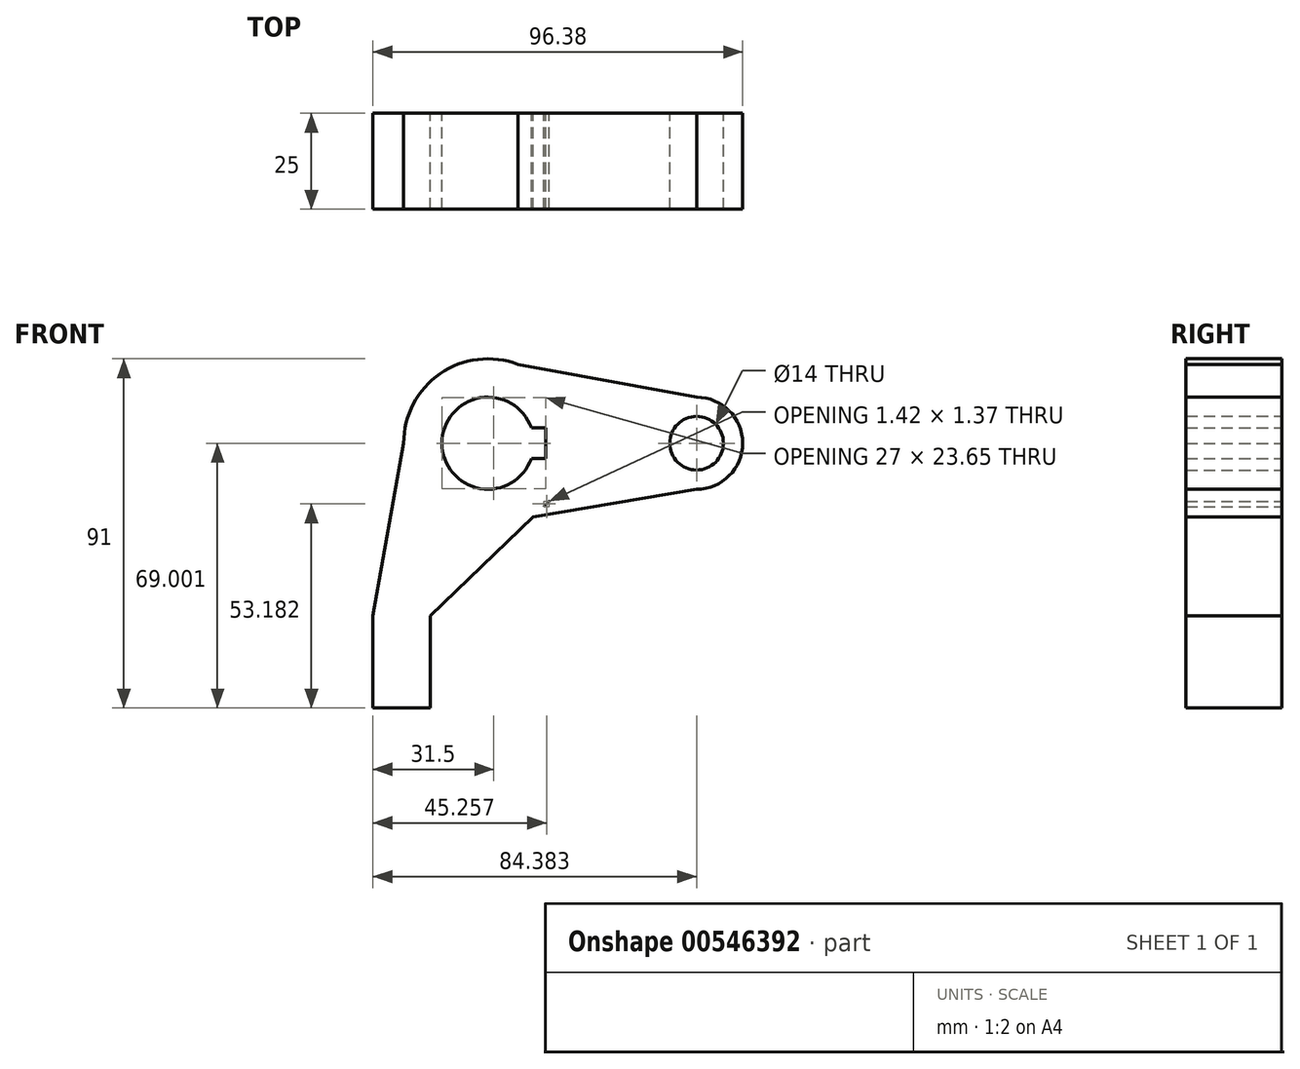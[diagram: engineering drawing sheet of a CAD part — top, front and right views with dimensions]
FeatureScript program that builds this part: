
annotation { "Feature Type Name" : "Feature", "Feature Type Description" : "" }
export const myFeature = defineFeature(function(context is Context, id is Id, definition is map)
    precondition{}
    {
        {
            var Q0;
            Q0=qCreatedBy(makeId("Front.planeOp"),FACE);
            var sketch = newSketch(context, id + "F0", { "sketchPlane" : qUnion([Q0])});
            skCircle(sketch, "E0", {"center": v(54.38, 46.5) * mm, "radius": 7 * mm});
            skCircle(sketch, "E1", {"center": v(54.38, 46.5) * mm, "radius": 12 * mm});
            skLineSegment(sketch, "E2", {"start": v(54.38, 74.2) * mm, "end": v(54.38, 10.91) * mm, "construction": true});
            skArc(sketch, "E3", {"start": v(11.31, 50.5) * mm, "mid": v(-12, 46.5) * mm, "end": v(11.31, 42.5) * mm});
            skCircle(sketch, "E4", {"center": v(0, 46.5) * mm, "radius": 22 * mm});
            skLineSegment(sketch, "E5", {"start": v(-12, 46.5) * mm, "end": v(15, 46.5) * mm, "construction": true});
            skLineSegment(sketch, "E6", {"start": v(15, 46.5) * mm, "end": v(15, 50.5) * mm});
            skLineSegment(sketch, "E7", {"start": v(15, 50.5) * mm, "end": v(11.31, 50.5) * mm});
            skLineSegment(sketch, "E8.MirrorCS", {"start": v(15, 46.5) * mm, "end": v(15, 42.5) * mm});
            skLineSegment(sketch, "E9.MirrorCS", {"start": v(15, 42.5) * mm, "end": v(11.31, 42.5) * mm});
            skLineSegment(sketch, "E10", {"start": v(54.38, 58.5) * mm, "end": v(0, 68.5) * mm});
            skLineSegment(sketch, "E11", {"start": v(0, 46.5) * mm, "end": v(0, -10.5) * mm, "construction": true});
            skLineSegment(sketch, "E12", {"start": v(-15, -22.5) * mm, "end": v(-30, -22.5) * mm});
            skLineSegment(sketch, "E13", {"start": v(-30, -22.5) * mm, "end": v(-30, 1.5) * mm});
            skLineSegment(sketch, "E14", {"start": v(-30, 1.5) * mm, "end": v(-15, 1.5) * mm});
            skLineSegment(sketch, "E15", {"start": v(-15, -22.5) * mm, "end": v(-15, -10.5) * mm});
            skLineSegment(sketch, "E16", {"start": v(-15, -10.5) * mm, "end": v(-15, 1.5) * mm});
            skLineSegment(sketch, "E17", {"start": v(-15, 1.5) * mm, "end": v(15.97, 31.37) * mm});
            skLineSegment(sketch, "E18", {"start": v(-30, 1.5) * mm, "end": v(-22, 46.5) * mm});
            skLineSegment(sketch, "E19", {"start": v(54.38, 34.5) * mm, "end": v(11.73, 27.28) * mm});
            skSolve(sketch);
        }
        {
            var Q0;
            Q0 = qSketchRegion(id + "F0", true);
            extrude(context, id + "F1", {"entities" : qUnion([Q0]), "depth" : 25 * mm, "offsetDistance" : 25 * mm});
        }
    });
